# Revit family: РВК_Муфта комбинированная НР
name_source: partatom
category: Соединительные детали трубопроводов
revit_build: Autodesk Revit 2016 (Build: 20150714_1515(x64)
units: mm (PartAtom-declared; Revit-internal decimal feet)

## family parameters
Всегда вертикально = Да
На основе рабочей плоскости = Нет
Общий = Нет
При загрузке вырезать с полостями = Нет
Размер круглого соединителя = Использовать радиус
Тип детали = Соединение

## types (8) — shared parameters
ADSK_Завод-изготовитель = РВК
K = 2 мм
Материал стальной части = РВК_Сталь хромированная
Материал фитинга = РВК_Полипропилен PPR

## per-type parameters (varying)
| type | A | B | C | D | DN | E | F | G | GN | H | I | J | L | M | N | O | R | T | U | g |
| Муфта комбинированная ПП D40-1'' НР | 22 мм | 53 мм | 26 мм | 40 мм | 40 мм | 24 мм | 2 мм | 25 мм | 32 мм | 11 мм | 5 мм | 2 мм | 48 мм | 11 мм | 54 мм | 53 мм | 20 мм | 18 мм | 14 мм | 16 мм |
| Муфта комбинированная ПП D32-1'' НР | 19 мм | 42 мм | 26 мм | 32 мм | 32 мм | 19 мм | 2 мм | 25 мм | 32 мм | 11 мм | 5 мм | 3 мм | 45 мм | 11 мм | 54 мм | 46 мм | 16 мм | 18 мм | 14 мм | 16 мм |
| Муфта комбинированная ПП D32-3/4'' НР | 19 мм | 42 мм | 18 мм | 32 мм | 32 мм | 19 мм | 2 мм | 20 мм | 25 мм | 11 мм | 5 мм | 3 мм | 40 мм | 11 мм | 46 мм | 46 мм | 16 мм | 15 мм | 12 мм | 13 мм |
| Муфта комбинированная ПП D25-3/4'' НР | 17 мм | 33 мм | 18 мм | 25 мм | 25 мм | 17 мм | 2 мм | 20 мм | 25 мм | 11 мм | 5 мм | 3 мм | 38 мм | 11 мм | 46 мм | 37 мм | 13 мм | 15 мм | 12 мм | 13 мм |
| Муфта комбинированная ПП D25-1/2'' НР | 17 мм | 33 мм | 14 мм | 25 мм | 25 мм | 17 мм | 2 мм | 15 мм | 20 мм | 10 мм | 5 мм | 3 мм | 36 мм | 11 мм | 38 мм | 38 мм | 13 мм | 15 мм | 12 мм | 10 мм |
| Муфта комбинированная ПП D20-3/4'' НР | 15 мм | 28 мм | 18 мм | 20 мм | 20 мм | 15 мм | 3 мм | 20 мм | 25 мм | 11 мм | 5 мм | 4 мм | 36 мм | 11 мм | 46 мм | 32 мм | 10 мм | 15 мм | 12 мм | 13 мм |
| Муфта комбинированная ПП D20-1/2'' НР | 15 мм | 28 мм | 18 мм | 20 мм | 20 мм | 14 мм | 2 мм | 15 мм | 20 мм | 14 мм | 5 мм | 4 мм | 33 мм | 12 мм | 36 мм | 32 мм | 10 мм | 15 мм | 12 мм | 10 мм |
| Муфта комбинированная ПП D16-1/2'' НР | 14 мм | 22 мм | 14 мм | 16 мм | 16 мм | 15 мм | 2 мм | 15 мм | 20 мм | 9 мм | 3 мм | 2 мм | 36 мм | 11 мм | 37 мм | 33 мм | 8 мм | 15 мм | 12 мм | 10 мм |

note: column(s) folded — value = type name in every type: Тип

## geometry (parser evidence)
native form markers: Blend x4
no freeform markers — native parametric forms only
